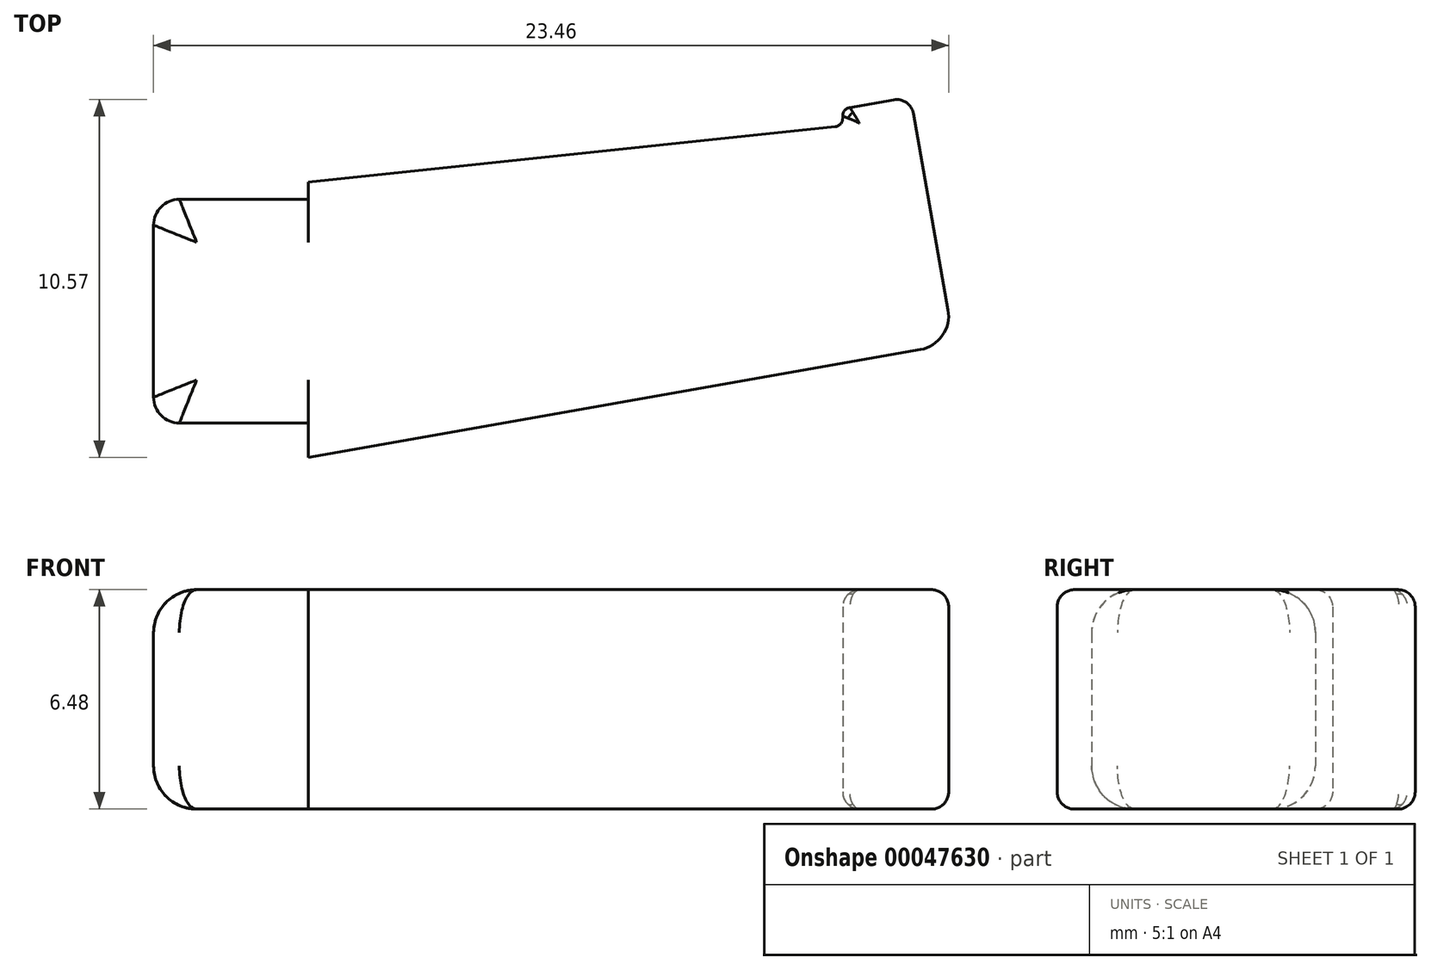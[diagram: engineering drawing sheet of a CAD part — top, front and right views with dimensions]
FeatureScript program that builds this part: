
annotation { "Feature Type Name" : "Feature", "Feature Type Description" : "" }
export const myFeature = defineFeature(function(context is Context, id is Id, definition is map)
    precondition{}
    {
        {
            var Q0;
            Q0=qCreatedBy(makeId("Top.planeOp"),FACE);
            var sketch = newSketch(context, id + "F0", { "sketchPlane" : qUnion([Q0])});
            skLineSegment(sketch, "E0", {"start": v(0, 0) * mm, "end": v(-3.81, 0) * mm});
            skLineSegment(sketch, "E1", {"start": v(-4.57, -0.76) * mm, "end": v(-4.57, -5.84) * mm});
            skLineSegment(sketch, "E2", {"start": v(-3.81, -6.6) * mm, "end": v(0, -6.6) * mm});
            skLineSegment(sketch, "E3", {"start": v(18.87, -3.26) * mm, "end": v(17.85, 2.53) * mm});
            skLineSegment(sketch, "E4", {"start": v(17.26, 2.94) * mm, "end": v(15.97, 2.7) * mm});
            skLineSegment(sketch, "E5", {"start": v(15.76, 2.46) * mm, "end": v(15.76, 2.4) * mm});
            skLineSegment(sketch, "E6", {"start": v(0, 0) * mm, "end": v(0, 0.5) * mm});
            skLineSegment(sketch, "E7", {"start": v(0, 0.5) * mm, "end": v(15.54, 2.14) * mm});
            skLineSegment(sketch, "E8", {"start": v(0, -6.6) * mm, "end": v(0, -7.62) * mm});
            skLineSegment(sketch, "E9", {"start": v(0, -7.62) * mm, "end": v(18.05, -4.44) * mm});
            skPoint(sketch, "E10.visualSharp", {"position": v(19.05, -4.26) * mm});
            skArc(sketch, "E10.filletArc", {"start": v(18.05, -4.44) * mm, "mid": v(18.7, -4.02) * mm, "end": v(18.87, -3.26) * mm});
            skPoint(sketch, "E11.visualSharp", {"position": v(15.76, 2.16) * mm});
            skArc(sketch, "E11.filletArc", {"start": v(15.54, 2.14) * mm, "mid": v(15.7, 2.22) * mm, "end": v(15.76, 2.4) * mm});
            skPoint(sketch, "E12.visualSharp", {"position": v(15.76, 2.67) * mm});
            skArc(sketch, "E12.filletArc", {"start": v(15.97, 2.7) * mm, "mid": v(15.82, 2.62) * mm, "end": v(15.76, 2.46) * mm});
            skPoint(sketch, "E13.visualSharp", {"position": v(17.77, 3.03) * mm});
            skArc(sketch, "E13.filletArc", {"start": v(17.85, 2.53) * mm, "mid": v(17.64, 2.85) * mm, "end": v(17.26, 2.94) * mm});
            skPoint(sketch, "E14.visualSharp", {"position": v(-4.57, 0) * mm});
            skArc(sketch, "E14.filletArc", {"start": v(-3.81, 0) * mm, "mid": v(-4.35, -0.22) * mm, "end": v(-4.57, -0.76) * mm});
            skPoint(sketch, "E15.visualSharp", {"position": v(-4.57, -6.6) * mm});
            skArc(sketch, "E15.filletArc", {"start": v(-4.57, -5.84) * mm, "mid": v(-4.35, -6.38) * mm, "end": v(-3.81, -6.6) * mm});
            skSolve(sketch);
        }
        {
            var Q0;
            Q0 = qSketchRegion(id + "F0", true);
            extrude(context, id + "F1", {"entities" : qUnion([Q0]), "depth" : 6.48 * mm});
        }
        {
            var Q0;
            Q0=makeQuery(id+"F1.opExtrude","CAP_EDGE",EDGE,{"disambiguationData":[OSD([sQuery(id+"F0.wireOp",EDGE,"E0")])],"isStart":false});
            var Q1;
            Q1=makeQuery(id+"F1.opExtrude","CAP_EDGE",EDGE,{"disambiguationData":[OSD([sQuery(id+"F0.wireOp",EDGE,"E0")])],"isStart":true});
            fillet(context, id + "F2", {"entities" : qUnion([Q0, Q1]), "radius" : 1.27 * mm, "tangentPropagation" : true, "allowEdgeOverflow" : false});
        }
        {
            var Q0;
            Q0=makeQuery(id+"F1.opExtrude","CAP_EDGE",EDGE,{"disambiguationData":[OSD([sQuery(id+"F0.wireOp",EDGE,"E7")])],"isStart":true});
            var Q1;
            Q1=makeQuery(id+"F1.opExtrude","CAP_EDGE",EDGE,{"disambiguationData":[OSD([sQuery(id+"F0.wireOp",EDGE,"E11.filletArc")])],"isStart":true});
            var Q2;
            Q2=makeQuery(id+"F1.opExtrude","CAP_EDGE",EDGE,{"disambiguationData":[OSD([sQuery(id+"F0.wireOp",EDGE,"E4")])],"isStart":true});
            var Q3;
            Q3=makeQuery(id+"F1.opExtrude","CAP_EDGE",EDGE,{"disambiguationData":[OSD([sQuery(id+"F0.wireOp",EDGE,"E13.filletArc")])],"isStart":true});
            var Q4;
            Q4=makeQuery(id+"F1.opExtrude","CAP_EDGE",EDGE,{"disambiguationData":[OSD([sQuery(id+"F0.wireOp",EDGE,"E3")])],"isStart":true});
            var Q5;
            Q5=makeQuery(id+"F1.opExtrude","CAP_EDGE",EDGE,{"disambiguationData":[OSD([sQuery(id+"F0.wireOp",EDGE,"E12.filletArc")])],"isStart":true});
            var Q6;
            Q6=makeQuery(id+"F1.opExtrude","CAP_EDGE",EDGE,{"disambiguationData":[OSD([sQuery(id+"F0.wireOp",EDGE,"E5")])],"isStart":true});
            fillet(context, id + "F3", {"entities" : qUnion([Q0, Q1, Q2, Q3, Q4, Q5, Q6]), "radius" : 0.5 * mm, "tangentPropagation" : true, "allowEdgeOverflow" : false});
        }
        {
            var Q0;
            Q0=makeQuery(id+"F1.opExtrude","CAP_EDGE",EDGE,{"disambiguationData":[OSD([sQuery(id+"F0.wireOp",EDGE,"E9")])],"isStart":false});
            fillet(context, id + "F4", {"entities" : qUnion([Q0]), "radius" : 0.5 * mm, "tangentPropagation" : true, "allowEdgeOverflow" : false});
        }
    });
